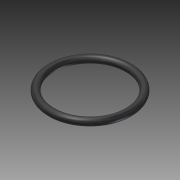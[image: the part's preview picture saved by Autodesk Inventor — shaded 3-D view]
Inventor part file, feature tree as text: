
AUTODESK INVENTOR PART (.ipt)
format: ipt  version: 2014 SP1 (Build 180222100, 222)  size: 103,424 bytes
history: native  units: in
note: dims shown in document units (in); Inventor stores cm internally (conversion verified against a paired STEP export)
features: revolve x1, sketch x1
ambient origin geometry x8: Origin, YZ Plane, XZ Plane, XY Plane, X Axis, Y Axis, Z Axis, Center Point
bodies: Solid1 (feature_tree)
feature tree (2):
  revolve  "Revolution1"  [1 undecoded]
  sketch  "Sketch1"  dims[d0=0.3438in d1=0.0625in d2=0.1in d3=90.0deg]
note: 1 required parameter value undecoded (feature->parameter linkage not recoverable at this tier; creation-order binding heuristic only, values carry confidence <= 0.55)
